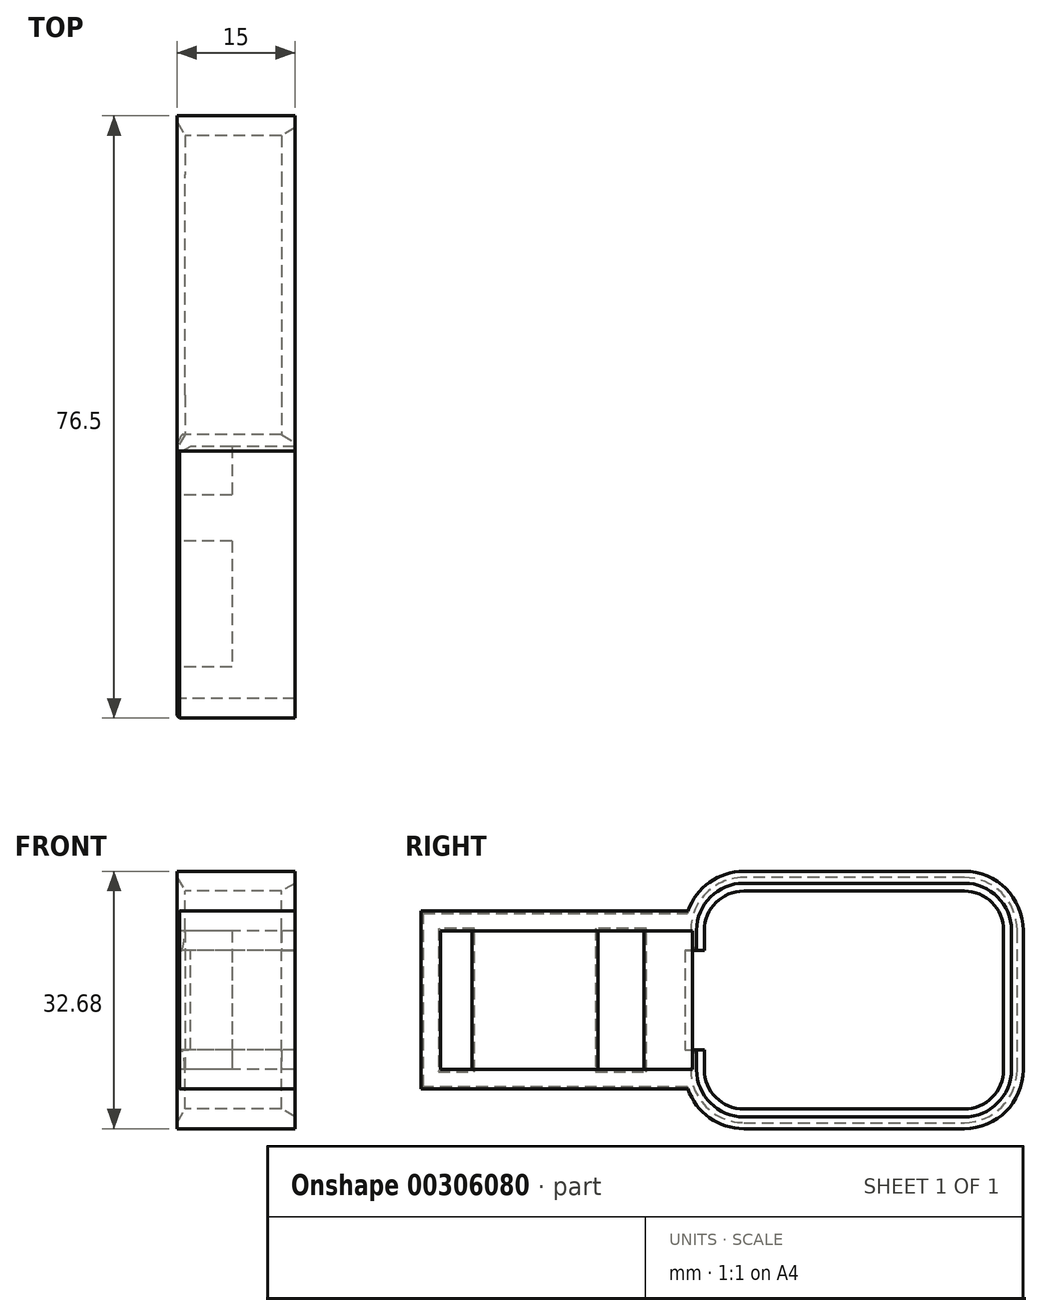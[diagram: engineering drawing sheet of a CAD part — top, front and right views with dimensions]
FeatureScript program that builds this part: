
annotation { "Feature Type Name" : "Feature", "Feature Type Description" : "" }
export const myFeature = defineFeature(function(context is Context, id is Id, definition is map)
    precondition{}
    {
        {
            var Q0;
            Q0=qCreatedBy(makeId("Right.planeOp"),FACE);
            var sketch = newSketch(context, id + "F0", { "sketchPlane" : qUnion([Q0])});
            skLineSegment(sketch, "E0.bottom", {"start": v(0, 0) * mm, "end": v(-32, 0) * mm});
            skLineSegment(sketch, "E0.top", {"start": v(0, 8.8) * mm, "end": v(-32, 8.8) * mm});
            skLineSegment(sketch, "E0.left", {"start": v(0, 0) * mm, "end": v(0, 8.8) * mm});
            skLineSegment(sketch, "E0.right", {"start": v(-32, 0) * mm, "end": v(-32, 8.8) * mm});
            skLineSegment(sketch, "E1.bottom", {"start": v(1.5, 0) * mm, "end": v(39.5, 0) * mm});
            skLineSegment(sketch, "E1.top", {"start": v(6.5, 13.84) * mm, "end": v(34.5, 13.84) * mm});
            skLineSegment(sketch, "E1.left", {"start": v(1.5, 0) * mm, "end": v(1.5, 8.84) * mm});
            skLineSegment(sketch, "E1.right", {"start": v(39.5, 0) * mm, "end": v(39.5, 8.84) * mm});
            skLineSegment(sketch, "E2.bottom", {"start": v(0, 6.31) * mm, "end": v(1.5, 6.31) * mm});
            skLineSegment(sketch, "E2.top", {"start": v(0, 0) * mm, "end": v(1.5, 0) * mm});
            skLineSegment(sketch, "E2.left", {"start": v(0, 6.31) * mm, "end": v(0, 0) * mm});
            skLineSegment(sketch, "E2.right", {"start": v(1.5, 6.31) * mm, "end": v(1.5, 0) * mm});
            skPoint(sketch, "E3.visualSharp", {"position": v(1.5, 13.84) * mm});
            skArc(sketch, "E3.filletArc", {"start": v(6.5, 13.84) * mm, "mid": v(2.96, 12.38) * mm, "end": v(1.5, 8.84) * mm});
            skPoint(sketch, "E4.visualSharp", {"position": v(39.5, 13.84) * mm});
            skArc(sketch, "E4.filletArc", {"start": v(39.5, 8.84) * mm, "mid": v(38.04, 12.38) * mm, "end": v(34.5, 13.84) * mm});
            skSolve(sketch);
        }
        {
            var Q0;
            Q0 = qSketchRegion(id + "F0", true);
            extrude(context, id + "F1", {"entities" : qUnion([Q0]), "depth" : 15 * mm, "offsetDistance" : 25 * mm});
        }
        {
            var Q0;
            Q0=makeQuery(id+"F1.opExtrude","SWEPT_BODY",BODY,{"disambiguationData":[OSD([sQuery(id+"F0.wireOp",EDGE,"E0.bottom"),sQuery(id+"F0.wireOp",EDGE,"E0.top"),sQuery(id+"F0.wireOp",EDGE,"E0.right"),sQuery(id+"F0.wireOp",EDGE,"MxC3bRiR-aJ8e-JiNF-EN7v-08XOjlkdgW0o.bottom"),sQuery(id+"F0.wireOp",EDGE,"MxC3bRiR-aJ8e-JiNF-EN7v-08XOjlkdgW0o.top"),sQuery(id+"F0.wireOp",EDGE,"MxC3bRiR-aJ8e-JiNF-EN7v-08XOjlkdgW0o.left"),sQuery(id+"F0.wireOp",EDGE,"MxC3bRiR-aJ8e-JiNF-EN7v-08XOjlkdgW0o.right"),sQuery(id+"F0.wireOp",EDGE,"b17bd446-9648-4086-a825-1f2499136baf.filletArc"),sQuery(id+"F0.wireOp",EDGE,"74f39944-9b35-4c1e-ac13-ccacfb9a023d.filletArc")])]});
            var Q1;
            Q1=makeQuery(id+"F1.opExtrude","SWEPT_FACE",FACE,{"disambiguationData":[OSD([sQuery(id+"F0.wireOp",EDGE,"E0.bottom"),sQuery(id+"F0.wireOp",EDGE,"MxC3bRiR-aJ8e-JiNF-EN7v-08XOjlkdgW0o.bottom")])]});
            mirror(context, id + "F2", {"operationType" : NewBodyOperationType.ADD, "entities" : qUnion([Q0]), "mirrorPlane" : qUnion([Q1])});
        }
        {
            var Q0;
            {var subQ0=makeQuery(id+"F1.opExtrude","CAP_FACE",FACE,{"disambiguationData":[OSD([sQuery(id+"F0.wireOp",EDGE,"E0.bottom"),sQuery(id+"F0.wireOp",EDGE,"E0.top"),sQuery(id+"F0.wireOp",EDGE,"E0.left"),sQuery(id+"F0.wireOp",EDGE,"E0.right"),sQuery(id+"F0.wireOp",EDGE,"E1.bottom"),sQuery(id+"F0.wireOp",EDGE,"E1.top"),sQuery(id+"F0.wireOp",EDGE,"E1.left"),sQuery(id+"F0.wireOp",EDGE,"E1.right"),sQuery(id+"F0.wireOp",EDGE,"E2.bottom"),sQuery(id+"F0.wireOp",EDGE,"E2.top"),sQuery(id+"F0.wireOp",EDGE,"E3.filletArc"),sQuery(id+"F0.wireOp",EDGE,"E4.filletArc")])],"isStart":false});Q0=makeQuery(id+"F2.boolean.opBoolean","MERGE",FACE,{"derivedFrom":[subQ0,makeQuery(id+"F2.opPattern","COPY",FACE,{"derivedFrom":subQ0,"instanceName":"1"})]});}
            var Q1;
            {var subQ0=makeQuery(id+"F1.opExtrude","CAP_FACE",FACE,{"disambiguationData":[OSD([sQuery(id+"F0.wireOp",EDGE,"E0.bottom"),sQuery(id+"F0.wireOp",EDGE,"E0.top"),sQuery(id+"F0.wireOp",EDGE,"E0.left"),sQuery(id+"F0.wireOp",EDGE,"E0.right"),sQuery(id+"F0.wireOp",EDGE,"E1.bottom"),sQuery(id+"F0.wireOp",EDGE,"E1.top"),sQuery(id+"F0.wireOp",EDGE,"E1.left"),sQuery(id+"F0.wireOp",EDGE,"E1.right"),sQuery(id+"F0.wireOp",EDGE,"E2.bottom"),sQuery(id+"F0.wireOp",EDGE,"E2.top"),sQuery(id+"F0.wireOp",EDGE,"E3.filletArc"),sQuery(id+"F0.wireOp",EDGE,"E4.filletArc")])],"isStart":true});Q1=makeQuery(id+"F2.boolean.opBoolean","MERGE",FACE,{"derivedFrom":[subQ0,makeQuery(id+"F2.opPattern","COPY",FACE,{"derivedFrom":subQ0,"instanceName":"1"})]});}
            shell(context, id + "F3", {"entities" : qUnion([Q0, Q1]), "thickness" : 2.5 * mm, "oppositeDirection" : true});
        }
        {
            var Q0;
            Q0=qCreatedBy(makeId("Right.planeOp"),FACE);
            var sketch = newSketch(context, id + "F4", { "sketchPlane" : qUnion([Q0])});
            skLineSegment(sketch, "E5.0", {"start": v(0, 8.8) * mm, "end": v(-32, 8.8) * mm});
            skLineSegment(sketch, "E6.0", {"start": v(-32, -8.8) * mm, "end": v(-32, 8.8) * mm});
            skLineSegment(sketch, "E7.0", {"start": v(0, -8.8) * mm, "end": v(-32, -8.8) * mm});
            skLineSegment(sketch, "E8", {"start": v(0, 8.8) * mm, "end": v(0, -8.8) * mm});
            skLineSegment(sketch, "E9", {"start": v(-28, 8.8) * mm, "end": v(-28, -8.8) * mm});
            skLineSegment(sketch, "E10.bottom", {"start": v(-12.02, 8.8) * mm, "end": v(-6.16, 8.8) * mm});
            skLineSegment(sketch, "E10.top", {"start": v(-12.02, -8.8) * mm, "end": v(-6.16, -8.8) * mm});
            skLineSegment(sketch, "E10.left", {"start": v(-12.02, 8.8) * mm, "end": v(-12.02, -8.8) * mm});
            skLineSegment(sketch, "E10.right", {"start": v(-6.16, 8.8) * mm, "end": v(-6.16, -8.8) * mm});
            skSolve(sketch);
        }
        {
            var Q0;
            {var subQ0=sQuery(id+"F4.wireOp",EDGE,"E9");Q0=makeQuery(id+"F4.imprint","IMPRINT",FACE,{"disambiguationData":[TD([[makeQuery(id+"F4.imprint","IMPRINT",EDGE,{"derivedFrom":subQ0}),1.0]])]});}
            var Q1;
            {var subQ0=sQuery(id+"F4.wireOp",EDGE,"E8");Q1=makeQuery(id+"F4.imprint","IMPRINT",FACE,{"disambiguationData":[TD([[makeQuery(id+"F4.imprint","IMPRINT",EDGE,{"derivedFrom":subQ0}),-1.0]])]});}
            extrude(context, id + "F5", {"entities" : qUnion([Q0, Q1]), "operationType" : NewBodyOperationType.ADD, "depth" : 7 * mm, "offsetDistance" : 25 * mm});
        }
        {
            var Q0;
            {var subQ0=sQuery(id+"F0.wireOp",EDGE,"E1.top");Q0=makeQuery(id+"F3.opShell","OFFSET_EDGE",EDGE,{"disambiguationData":[OSD([subQ0]),TDD([makeQuery(id+"F1.opExtrude","CAP_EDGE",EDGE,{"disambiguationData":[OSD([subQ0])],"isStart":false})])]});}
            var Q1;
            {var subQ0=sQuery(id+"F0.wireOp",EDGE,"E3.filletArc");Q1=makeQuery(id+"F3.opShell","OFFSET_EDGE",EDGE,{"disambiguationData":[OSD([subQ0]),TDD([makeQuery(id+"F2.opPattern","COPY",EDGE,{"derivedFrom":makeQuery(id+"F1.opExtrude","CAP_EDGE",EDGE,{"disambiguationData":[OSD([subQ0])],"isStart":true}),"instanceName":"1"})])]});}
            var Q2;
            Q2=makeQuery(id+"F5.opExtrude","CAP_EDGE",EDGE,{"disambiguationData":[OSD([sQuery(id+"F4.wireOp",EDGE,"E8")])],"isStart":true});
            chamfer(context, id + "F6", {"entities" : qUnion([Q0, Q1, Q2]), "chamferType" : ChamferType.OFFSET_ANGLE, "width" : 1 * mm, "oppositeDirection" : false, "angle" : 60 * degree, "tangentPropagation" : true});
        }
        {
            var Q0;
            Q0=makeQuery(id+"F2.opPattern","COPY",EDGE,{"derivedFrom":makeQuery(id+"F1.opExtrude","CAP_EDGE",EDGE,{"disambiguationData":[OSD([sQuery(id+"F0.wireOp",EDGE,"E0.top")])],"isStart":true}),"instanceName":"1"});
            var Q1;
            {var subQ0=makeQuery(id+"F1.opExtrude","CAP_EDGE",EDGE,{"disambiguationData":[OSD([sQuery(id+"F0.wireOp",EDGE,"E0.right")])],"isStart":true});Q1=makeQuery(id+"F2.boolean.opBoolean","MERGE",EDGE,{"derivedFrom":[subQ0,makeQuery(id+"F2.opPattern","COPY",EDGE,{"derivedFrom":subQ0,"instanceName":"1"})]});}
            var Q2;
            Q2=makeQuery(id+"F1.opExtrude","CAP_EDGE",EDGE,{"disambiguationData":[OSD([sQuery(id+"F0.wireOp",EDGE,"E0.top")])],"isStart":true});
            var Q3;
            Q3=makeQuery(id+"F5.opExtrude","CAP_EDGE",EDGE,{"disambiguationData":[OSD([sQuery(id+"F4.wireOp",EDGE,"E10.left")])],"isStart":true});
            var Q4;
            Q4=makeQuery(id+"F5.opExtrude","CAP_EDGE",EDGE,{"disambiguationData":[OSD([sQuery(id+"F4.wireOp",EDGE,"E10.right")])],"isStart":true});
            var Q5;
            {var subQ3=sQuery(id+"F0.wireOp",EDGE,"E0.top");var subQ5=sQuery(id+"F4.wireOp",EDGE,"E10.left");Q5=makeQuery(id+"F5.boolean.opBoolean","SPLIT",EDGE,{"disambiguationData":[TD([makeQuery(id+"F5.opExtrude","SWEPT_FACE",FACE,{"disambiguationData":[OSD([subQ5])]})])],"derivedFrom":makeQuery(id+"F3.opShell","OFFSET_EDGE",EDGE,{"disambiguationData":[OSD([subQ3]),TDD([makeQuery(id+"F2.opPattern","COPY",EDGE,{"derivedFrom":makeQuery(id+"F1.opExtrude","CAP_EDGE",EDGE,{"disambiguationData":[OSD([subQ3])],"isStart":true}),"instanceName":"1"})])]})});}
            var Q6;
            {var subQ3=sQuery(id+"F0.wireOp",EDGE,"E0.top");var subQ4=sQuery(id+"F4.wireOp",EDGE,"E10.left");Q6=makeQuery(id+"F5.boolean.opBoolean","SPLIT",EDGE,{"disambiguationData":[TD([makeQuery(id+"F5.opExtrude","SWEPT_FACE",FACE,{"disambiguationData":[OSD([subQ4])]})])],"derivedFrom":makeQuery(id+"F3.opShell","OFFSET_EDGE",EDGE,{"disambiguationData":[OSD([subQ3]),TDD([makeQuery(id+"F1.opExtrude","CAP_EDGE",EDGE,{"disambiguationData":[OSD([subQ3])],"isStart":true})])]})});}
            var Q7;
            Q7=makeQuery(id+"F5.opExtrude","CAP_EDGE",EDGE,{"disambiguationData":[OSD([sQuery(id+"F4.wireOp",EDGE,"E9")])],"isStart":true});
            var Q8;
            {var subQ0=sQuery(id+"F0.wireOp",EDGE,"E0.right");var subQ1=sQuery(id+"F0.wireOp",EDGE,"E0.top");Q8=makeQuery(id+"F5.boolean.opBoolean","SPLIT",EDGE,{"disambiguationData":[TD([makeQuery(id+"F3.opShell","OFFSET_FACE",FACE,{"disambiguationData":[OSD([subQ0])]})])],"derivedFrom":makeQuery(id+"F3.opShell","OFFSET_EDGE",EDGE,{"disambiguationData":[OSD([subQ1]),TDD([makeQuery(id+"F2.opPattern","COPY",EDGE,{"derivedFrom":makeQuery(id+"F1.opExtrude","CAP_EDGE",EDGE,{"disambiguationData":[OSD([subQ1])],"isStart":true}),"instanceName":"1"})])]})});}
            var Q9;
            {var subQ0=sQuery(id+"F0.wireOp",EDGE,"E0.right");var subQ1=makeQuery(id+"F1.opExtrude","CAP_EDGE",EDGE,{"disambiguationData":[OSD([subQ0])],"isStart":true});Q9=makeQuery(id+"F3.opShell","OFFSET_EDGE",EDGE,{"disambiguationData":[OSD([subQ0]),TDD([makeQuery(id+"F2.boolean.opBoolean","MERGE",EDGE,{"derivedFrom":[subQ1,makeQuery(id+"F2.opPattern","COPY",EDGE,{"derivedFrom":subQ1,"instanceName":"1"})]})])]});}
            var Q10;
            {var subQ0=sQuery(id+"F0.wireOp",EDGE,"E0.right");var subQ1=sQuery(id+"F0.wireOp",EDGE,"E0.top");Q10=makeQuery(id+"F5.boolean.opBoolean","SPLIT",EDGE,{"disambiguationData":[TD([makeQuery(id+"F3.opShell","OFFSET_FACE",FACE,{"disambiguationData":[OSD([subQ0])]})])],"derivedFrom":makeQuery(id+"F3.opShell","OFFSET_EDGE",EDGE,{"disambiguationData":[OSD([subQ1]),TDD([makeQuery(id+"F1.opExtrude","CAP_EDGE",EDGE,{"disambiguationData":[OSD([subQ1])],"isStart":true})])]})});}
            chamfer(context, id + "F7", {"entities" : qUnion([Q0, Q1, Q2, Q3, Q4, Q5, Q6, Q7, Q8, Q9, Q10]), "width" : 0.3 * mm, "tangentPropagation" : true});
        }
    });
